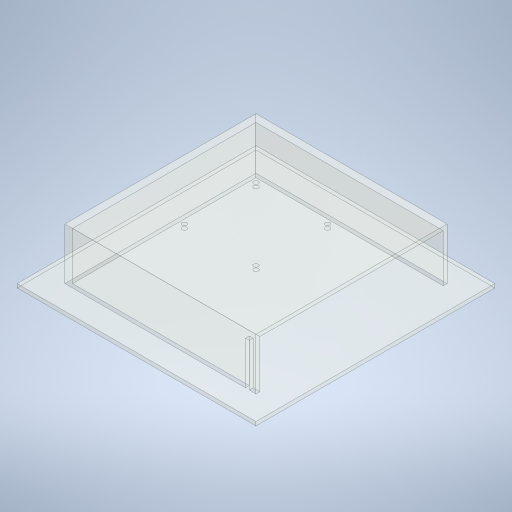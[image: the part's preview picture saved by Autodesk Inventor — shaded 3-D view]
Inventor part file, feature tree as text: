
AUTODESK INVENTOR PART (.ipt)
format: ipt  version: 2024 (Build 280153000, 153)  size: 294,912 bytes
history: native  units: in
note: dims shown in document units (in); Inventor stores cm internally (conversion verified against a paired STEP export)
features: sketch x6, extrude x5, hole x1
ambient origin geometry x8: Origin, YZ Plane, XZ Plane, XY Plane, X Axis, Y Axis, Z Axis, Center Point
bodies: Solid1 (feature_tree)
feature tree (12):
  extrude  "Main Body Extrusion"  Depth=7.5591in
  extrude  "Extrusion3"  Depth=7.874in
  extrude  "Extrusion8"  Depth=0.1575in
  extrude  "Extrusion9"  Depth=0.1575in
  extrude  "Extrusion10"  Depth=1.7717in TaperAngle=0.0deg
  hole  "Hole1"  [1 undecoded]
  sketch  "Sketch1"  dims[d13=1.9685in d14=0.0in d16=7.5591in]
  sketch  "Sketch3"  dims[d17=7.874in d18=7.874in]
  sketch  "Sketch8"  dims[d35=0.0787in d36=0.0in d39=0.1575in]
  sketch  "Sketch9"  dims[d40=7.2835in d41=0.1575in]
  sketch  "Sketch10"  dims[d42=1.7717in d43=0.0787in d44=0.0in]
  sketch  "Sketch11"  dims[d45=0.1575in d46=0.0in d47=0.1575in d48=0.1575in d49=0.1969in d50=0.2953in d51=0.1476in d52=0.0984in d53=90.0deg d54=0.3937in d55=0.0in d56=3.937in d57=3.937in d58=0.4921in d59=0.4921in d60=1.5748in d62=360.0deg]
note: 1 required parameter value undecoded (feature->parameter linkage not recoverable at this tier; creation-order binding heuristic only, values carry confidence <= 0.55)
